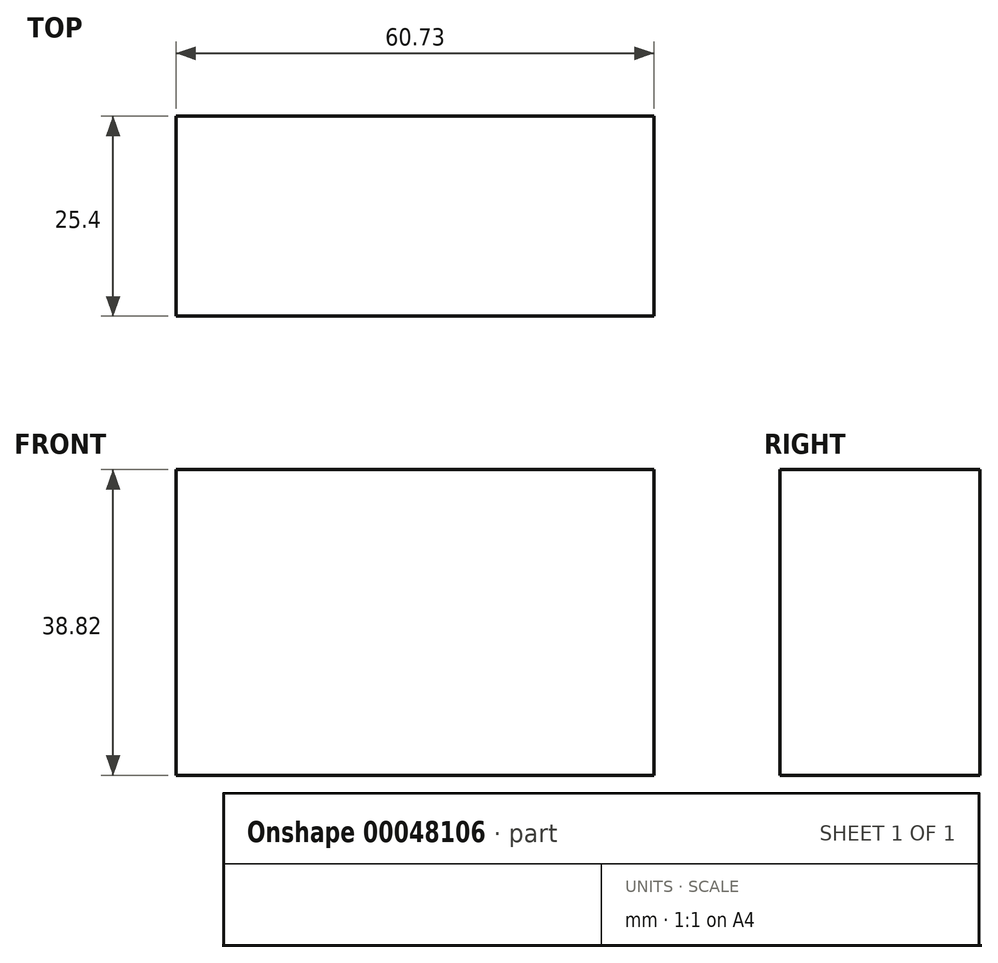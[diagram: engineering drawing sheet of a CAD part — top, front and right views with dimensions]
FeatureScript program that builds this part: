
annotation { "Feature Type Name" : "Feature", "Feature Type Description" : "" }
export const myFeature = defineFeature(function(context is Context, id is Id, definition is map)
    precondition{}
    {
        {
            var Q0;
            Q0=qCreatedBy(makeId("Front.planeOp"),FACE);
            var sketch = newSketch(context, id + "F0", { "sketchPlane" : qUnion([Q0])});
            skLineSegment(sketch, "E0.bottom", {"start": v(-32.08, 0) * mm, "end": v(28.65, 0) * mm});
            skLineSegment(sketch, "E0.top", {"start": v(-32.08, 38.82) * mm, "end": v(28.65, 38.82) * mm});
            skLineSegment(sketch, "E0.left", {"start": v(-32.08, 0) * mm, "end": v(-32.08, 38.82) * mm});
            skLineSegment(sketch, "E0.right", {"start": v(28.65, 0) * mm, "end": v(28.65, 38.82) * mm});
            skSolve(sketch);
        }
        {
            var Q0;
            Q0=makeQuery(id+"F0.imprint","IMPRINT",FACE,{"disambiguationData":[TD([[makeQuery(id+"F0.imprint","IMPRINT",EDGE,{"derivedFrom":sQuery(id+"F0.wireOp",EDGE,"E0.bottom")}),1.0]])]});
            extrude(context, id + "F1", {"entities" : qUnion([Q0]), "depth" : 25.4 * mm});
        }
    });
